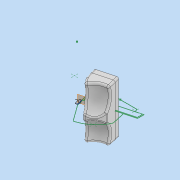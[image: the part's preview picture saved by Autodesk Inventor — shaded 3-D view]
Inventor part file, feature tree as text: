
AUTODESK INVENTOR PART (.ipt)
format: ipt  version: 2022 (Build 260153070, 153G)  size: 884,224 bytes
history: native  units: mm
features: other x29, surface_op x20, sketch x4, extrude x2, projected_geometry x2, plane x1, fillet x1, mirror x1, pattern_linear x1
ambient origin geometry x8: Origin, YZ Plane, XZ Plane, XY Plane, X Axis, Y Axis, Z Axis, Center Point
bodies: Body1 (feature_tree), Body2 (feature_tree), Body3 (feature_tree), Body4 (feature_tree), Body5 (feature_tree), Body6 (feature_tree), Body7 (feature_tree), Body8 (feature_tree), Body9 (feature_tree), Body10 (feature_tree), Body11 (feature_tree), Body12 (feature_tree), Body13 (feature_tree), Body14 (feature_tree)
feature tree (61):
  other  "P00173-09-015.ipt"
  other  "P00173-09-005.ipt"
  other  "Blocks"
  plane  "Work Plane8"
  surface_op  "Trim1"
  surface_op  "Trim2"
  surface_op  "Trim3"
  surface_op  "Trim4"
  surface_op  "Trim5"
  surface_op  "Trim6"
  surface_op  "Trim7"
  surface_op  "Trim8"
  surface_op  "Trim9"
  surface_op  "Trim10"
  surface_op  "Stitch Surface1"
  surface_op  "Trim11"
  surface_op  "Trim12"
  surface_op  "Stitch Surface2"
  fillet  "Fillet1"  Radius=10.0mm
  sketch  "Sketch16"  dims[d1=15.0mm d2=20.0mm d3=20.0mm d4=10.0mm d7=0.0mm d10=3.7mm d12=127.25mm d13=0.0mm d14=200.0mm d15=0.0mm d16=120.0deg d17=120.0deg d18=5.0mm d19=5.0mm d20=8.0mm d24=18.326338mm d25=6.0mm d26=140.0mm d27=0.0mm d28=15.0mm d29=120.0deg d30=50.0mm d31=0.0mm d36=1.25mm d40=5.0mm d41=8.0mm d42=5.0mm d43=4.0mm d44=1.0mm d45=1.0mm d46=65.0mm d47=0.0mm d48=1.745329mm d49=2.0mm d50=5.0mm d51=45.0mm d52=50.0mm d53=70.0mm d55=120.0mm d56=12.0mm d57=15.0mm d58=8.0mm d60=50.0mm d62=20.0mm d63=65.0mm d64=0.349066mm d23=18.326338mm d187=8.0mm d188=24.0mm d189=25.0mm d194=9.5mm d201=21.0mm d202=2.0mm d203=12.5mm d204=2.1mm d5=10.0mm]
  surface_op  "Extend1"
  surface_op  "Trim13"
  surface_op  "Stitch Surface3"
  mirror  "Mirror1"
  surface_op  "Stitch Surface5"
  extrude  "Extrusion1"  Depth=10.0mm
  extrude  "Extrusion2"  Depth=20.0mm
  pattern_linear  "Rectangular Pattern1"  Count1=2  [1 undecoded]
  other  "TaggingFeature1"
  other  "Camera_Top"
  other  "Block2"
  other  "Camera_Top_2"
  other  "Srf15"
  other  "Srf17"
  other  "Srf18"
  other  "Srf19"
  other  "Srf20"
  other  "Srf21"
  other  "Side"
  other  "Srf22"
  other  "Srf23"
  other  "Srf24"
  sketch  "Sketch17"  dims[d6=20.0mm d8=20.0mm d9=20.0mm]
  other  "Srf25"
  other  "Srf26"
  other  "Srf27"
  sketch  "Sketch18"  dims[d11=20.0mm]
  sketch  "Sketch19"  dims[d21=20.0mm d22=20.0mm d32=20.0mm d33=15.0mm d34=20.0mm d35=5.0mm d37=6.0mm d38=15.0mm d39=0.0mm d54=2.5mm d59=5.0mm d61=15.0mm d65=0.0mm d66=60.0mm d68=10.0mm d69=30.0mm d71=75.0mm]
  other  "OffsetSrf1"
  other  "OffsetSrf2"
  other  "OffsetSrf3"
  other  "OffsetSrf4"
  other  "Solid5::P00173-09-015.ipt"
  other  "Srf3"
  other  "Srf6::Derived"
  other  "Srf1::Derived"
  other  "Srf8::Derived"
  projected_geometry  "Project Cut Edges1"
  surface_op  "Stitch Surface4"
  projected_geometry  "Project Cut Edges2"
  surface_op  "Boundary Patch1"
note: 1 required parameter value undecoded (feature->parameter linkage not recoverable at this tier; creation-order binding heuristic only, values carry confidence <= 0.55)
